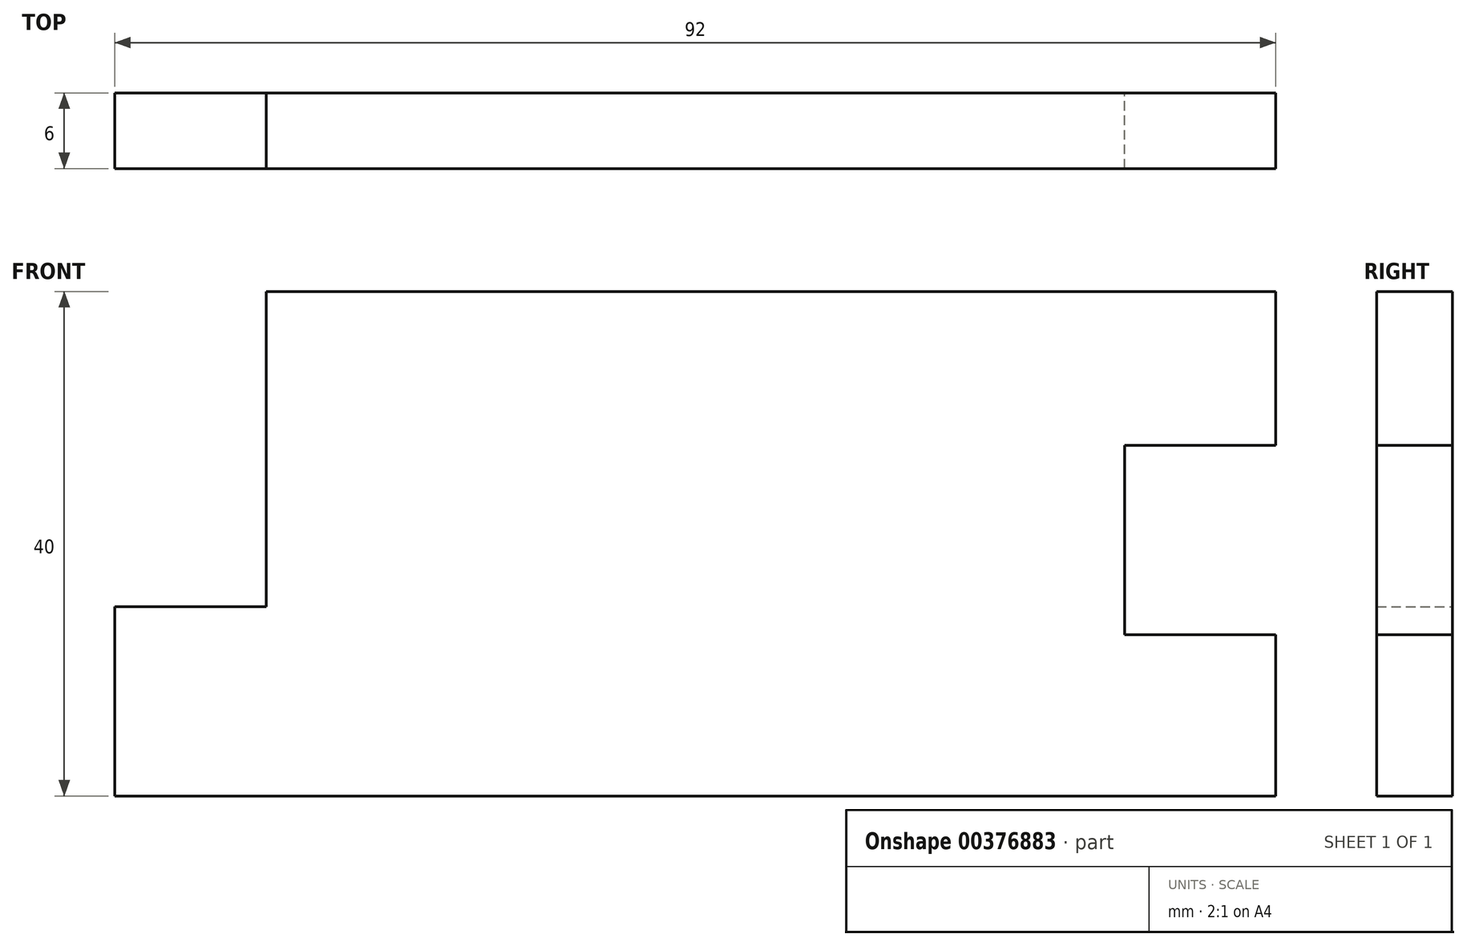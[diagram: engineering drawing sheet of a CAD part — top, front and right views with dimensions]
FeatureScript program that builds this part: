
annotation { "Feature Type Name" : "Feature", "Feature Type Description" : "" }
export const myFeature = defineFeature(function(context is Context, id is Id, definition is map)
    precondition{}
    {
        {
            var Q0;
            Q0=qCreatedBy(makeId("Front.planeOp"),FACE);
            var sketch = newSketch(context, id + "F0", { "sketchPlane" : qUnion([Q0])});
            skLineSegment(sketch, "E0.bottom", {"start": v(0, 0) * mm, "end": v(80, 0) * mm});
            skLineSegment(sketch, "E0.top", {"start": v(0, 40) * mm, "end": v(80, 40) * mm});
            skLineSegment(sketch, "E0.left", {"start": v(0, 15) * mm, "end": v(0, 40) * mm});
            skLineSegment(sketch, "E0.right", {"start": v(80, 0) * mm, "end": v(80, 12.79) * mm});
            skLineSegment(sketch, "E1", {"start": v(0, 0) * mm, "end": v(-12, 0) * mm});
            skLineSegment(sketch, "E2", {"start": v(-12, 0) * mm, "end": v(-12, 15) * mm});
            skLineSegment(sketch, "E3", {"start": v(-12, 15) * mm, "end": v(0, 15) * mm});
            skLineSegment(sketch, "E4", {"start": v(80, 27.79) * mm, "end": v(68, 27.79) * mm});
            skLineSegment(sketch, "E5", {"start": v(68, 27.79) * mm, "end": v(68, 12.79) * mm});
            skLineSegment(sketch, "E6", {"start": v(68, 12.79) * mm, "end": v(80, 12.79) * mm});
            skLineSegment(sketch, "E7.trimOffspring", {"start": v(80, 27.79) * mm, "end": v(80, 40) * mm});
            skSolve(sketch);
        }
        {
            var Q0;
            Q0=makeQuery(id+"F0.imprint","IMPRINT",FACE,{"disambiguationData":[TD([[makeQuery(id+"F0.imprint","IMPRINT",EDGE,{"derivedFrom":sQuery(id+"F0.wireOp",EDGE,"E0.bottom")}),1.0]])]});
            extrude(context, id + "F1", {"entities" : qUnion([Q0]), "depth" : 6 * mm});
        }
    });
